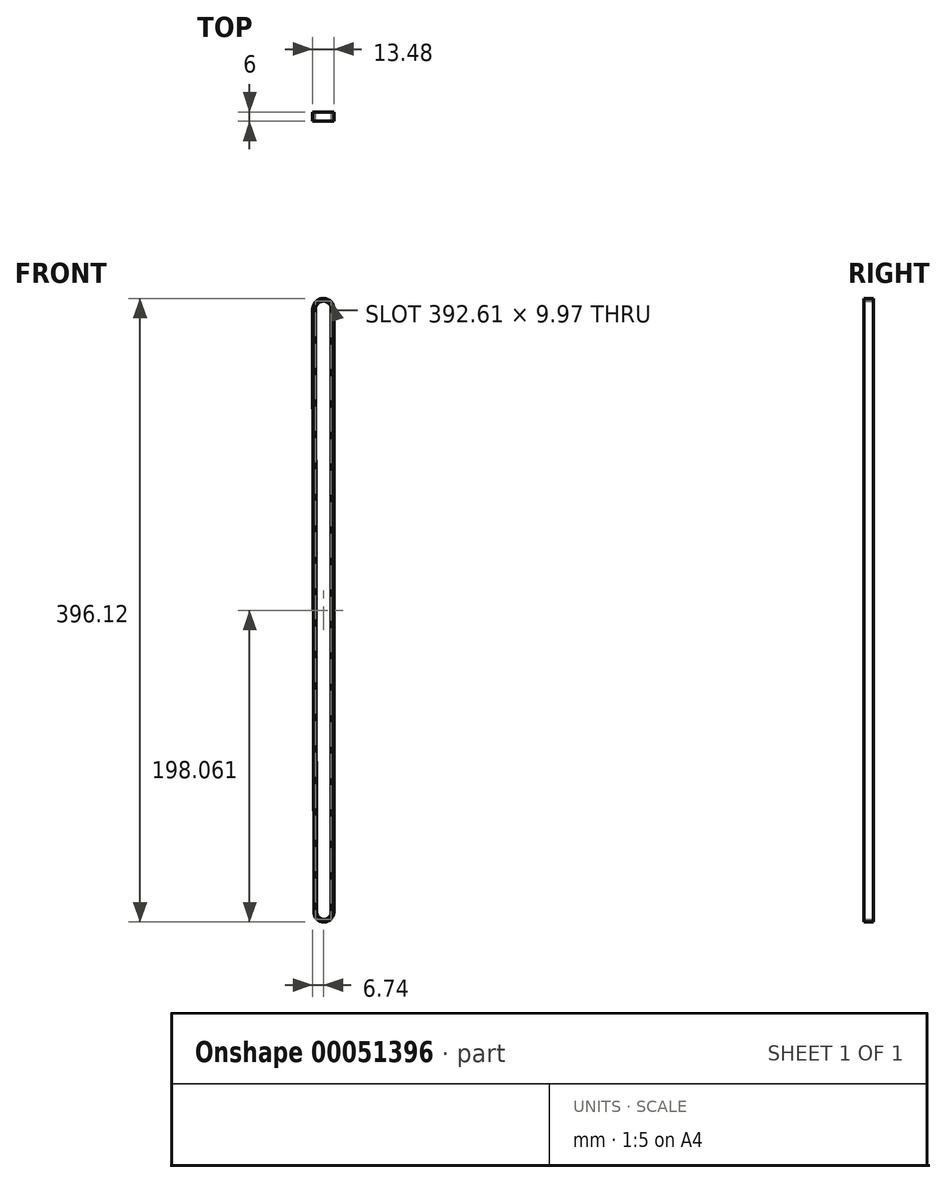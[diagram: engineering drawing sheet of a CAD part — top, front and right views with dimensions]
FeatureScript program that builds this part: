
annotation { "Feature Type Name" : "Feature", "Feature Type Description" : "" }
export const myFeature = defineFeature(function(context is Context, id is Id, definition is map)
    precondition{}
    {
        {
            var Q0;
            Q0=qCreatedBy(makeId("Front.planeOp"),FACE);
            var sketch = newSketch(context, id + "F0", { "sketchPlane" : qUnion([Q0])});
            skArc(sketch, "E0", {"start": v(6.37, 0) * mm, "mid": v(0, 6.37) * mm, "end": v(-6.37, -0.01) * mm});
            skLineSegment(sketch, "E1", {"start": v(0, 0) * mm, "end": v(0, -383) * mm, "construction": true});
            skLineSegment(sketch, "E2", {"start": v(6.37, 0) * mm, "end": v(6.37, -383) * mm});
            skCircle(sketch, "E3", {"center": v(0.36, -383) * mm, "radius": 5 * mm, "construction": true});
            skLineSegment(sketch, "E4", {"start": v(0, -383) * mm, "end": v(0.36, -383) * mm, "construction": true});
            skLineSegment(sketch, "E5", {"start": v(0.36, -383) * mm, "end": v(5.36, -383) * mm, "construction": true});
            skLineSegment(sketch, "E6", {"start": v(5.36, -383) * mm, "end": v(6.37, -383) * mm, "construction": true});
            skArc(sketch, "E7", {"start": v(-5.64, -383.01) * mm, "mid": v(0.37, -389) * mm, "end": v(6.37, -383) * mm});
            skLineSegment(sketch, "E8", {"start": v(-6.37, -0.01) * mm, "end": v(-5.64, -383.01) * mm});
            skLineSegment(sketch, "E9", {"start": v(-6.37, -0.01) * mm, "end": v(-6.37, -383) * mm, "construction": true});
            skSolve(sketch);
        }
        {
            var Q0;
            Q0=qCreatedBy(makeId("Top.planeOp"),FACE);
            var sketch = newSketch(context, id + "F1", { "sketchPlane" : qUnion([Q0])});
            skLineSegment(sketch, "E10.bottom", {"start": v(4.99, 3) * mm, "end": v(6.74, 3) * mm});
            skLineSegment(sketch, "E10.top", {"start": v(4.99, -3) * mm, "end": v(6.74, -3) * mm});
            skLineSegment(sketch, "E10.left", {"start": v(4.99, 3) * mm, "end": v(4.99, -3) * mm});
            skLineSegment(sketch, "E10.right", {"start": v(6.74, 3) * mm, "end": v(6.74, -3) * mm});
            skLineSegment(sketch, "E11", {"start": v(4.99, 0) * mm, "end": v(6.37, 0) * mm, "construction": true});
            skLineSegment(sketch, "E12", {"start": v(6.37, 0) * mm, "end": v(6.74, 0) * mm, "construction": true});
            skSolve(sketch);
        }
        {
            var Q0;
            Q0 = qSketchRegion(id + "F1", true);
            var Q1;
            Q1 = qConstructionFilter(qBodyType(qCreatedBy(id + "F0" ,EDGE), BodyType.WIRE), ConstructionObject.NO);
            sweep(context, id + "F2", {"profiles" : qUnion([Q0]), "path" : qUnion([Q1])});
        }
    });
